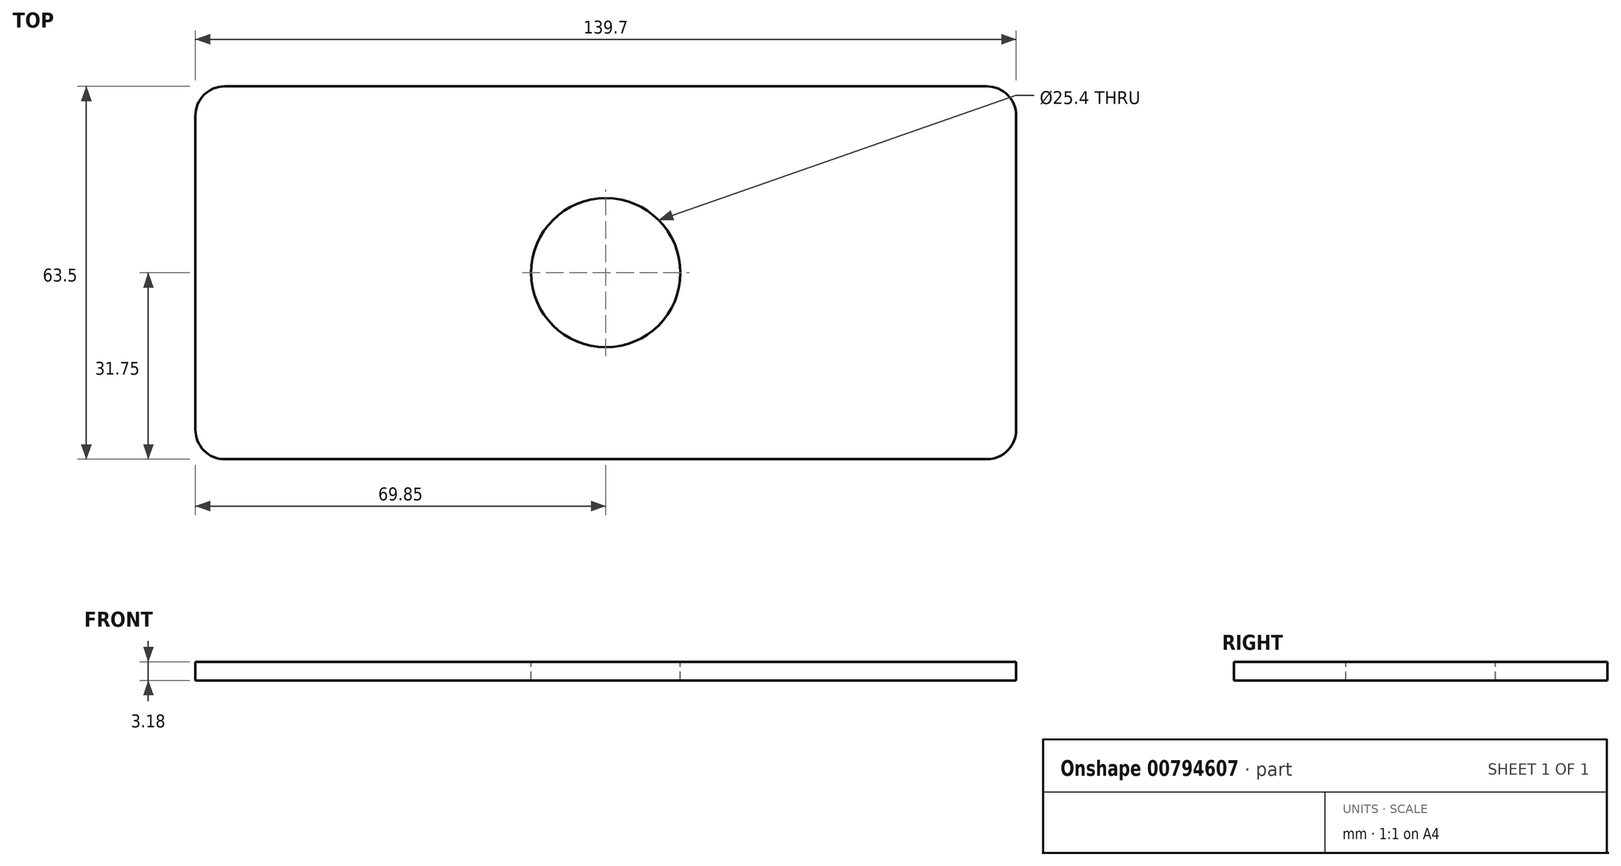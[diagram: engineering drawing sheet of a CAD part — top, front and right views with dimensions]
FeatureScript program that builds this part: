
annotation { "Feature Type Name" : "Feature", "Feature Type Description" : "" }
export const myFeature = defineFeature(function(context is Context, id is Id, definition is map)
    precondition{}
    {
        {
            var Q0;
            Q0=qCreatedBy(makeId("Top.planeOp"),FACE);
            var sketch = newSketch(context, id + "F0", { "sketchPlane" : qUnion([Q0])});
            skLineSegment(sketch, "E0.bottom", {"start": v(64.85, 31.75) * mm, "end": v(-64.85, 31.75) * mm});
            skLineSegment(sketch, "E0.top", {"start": v(64.85, -31.75) * mm, "end": v(-64.85, -31.75) * mm});
            skLineSegment(sketch, "E0.left", {"start": v(69.85, 26.75) * mm, "end": v(69.85, -26.75) * mm});
            skLineSegment(sketch, "E0.right", {"start": v(-69.85, 26.75) * mm, "end": v(-69.85, -26.75) * mm});
            skPoint(sketch, "E0.middle", {"position": v(0, 0) * mm});
            skPoint(sketch, "E1.visualSharp", {"position": v(69.85, -31.75) * mm});
            skArc(sketch, "E1.filletArc", {"start": v(64.85, -31.75) * mm, "mid": v(68.39, -30.29) * mm, "end": v(69.85, -26.75) * mm});
            skPoint(sketch, "E2.visualSharp", {"position": v(69.85, 31.75) * mm});
            skArc(sketch, "E2.filletArc", {"start": v(69.85, 26.75) * mm, "mid": v(68.39, 30.29) * mm, "end": v(64.85, 31.75) * mm});
            skPoint(sketch, "E3.visualSharp", {"position": v(-69.85, 31.75) * mm});
            skArc(sketch, "E3.filletArc", {"start": v(-64.85, 31.75) * mm, "mid": v(-68.39, 30.29) * mm, "end": v(-69.85, 26.75) * mm});
            skPoint(sketch, "E4.visualSharp", {"position": v(-69.85, -31.75) * mm});
            skArc(sketch, "E4.filletArc", {"start": v(-69.85, -26.75) * mm, "mid": v(-68.39, -30.29) * mm, "end": v(-64.85, -31.75) * mm});
            skSolve(sketch);
        }
        {
            var Q0;
            Q0 = qSketchRegion(id + "F0", true);
            extrude(context, id + "F1", {"entities" : qUnion([Q0]), "depth" : 3.17 * mm, "offsetDistance" : 25 * mm});
        }
        {
            var Q0;
            Q0=makeQuery(id+"F1.opExtrude","CAP_FACE",FACE,{"disambiguationData":[OSD([sQuery(id+"F0.wireOp",EDGE,"E0.bottom"),sQuery(id+"F0.wireOp",EDGE,"E0.top"),sQuery(id+"F0.wireOp",EDGE,"E0.left"),sQuery(id+"F0.wireOp",EDGE,"E0.right"),sQuery(id+"F0.wireOp",EDGE,"E1.filletArc"),sQuery(id+"F0.wireOp",EDGE,"E2.filletArc"),sQuery(id+"F0.wireOp",EDGE,"E3.filletArc"),sQuery(id+"F0.wireOp",EDGE,"E4.filletArc")])],"isStart":false});
            var sketch = newSketch(context, id + "F2", { "sketchPlane" : qUnion([Q0])});
            skCircle(sketch, "E5", {"center": v(0, 0) * mm, "radius": 12.7 * mm});
            skSolve(sketch);
        }
        {
            var Q0;
            Q0 = qSketchRegion(id + "F2", true);
            extrude(context, id + "F3", {"entities" : qUnion([Q0]), "operationType" : NewBodyOperationType.REMOVE, "endBound" : BoundingType.THROUGH_ALL, "oppositeDirection" : true, "depth" : 25 * mm, "offsetDistance" : 25 * mm});
        }
    });
